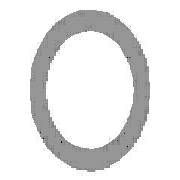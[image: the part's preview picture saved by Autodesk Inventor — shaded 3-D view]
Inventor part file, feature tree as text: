
AUTODESK INVENTOR PART (.ipt)
format: ipt  version: 2024.3 (Build 283343000, 343)  size: 162,304 bytes
history: native  units: mm (DEFAULTED — no unit token found)
features: other x5, sweep x1, sketch x1, plane x1
ambient origin geometry x8: Origin, YZ Plane, XZ Plane, XY Plane, X Axis, Y Axis, Z Axis, Center Point
bodies: Solid1 (feature_tree), Body (feature_tree)
feature tree (8):
  parser-record x1  (decoder bookkeeping rows leaked as tree rows — omitted from the tree; the rows remain in map.json)
  other  "Driven Length"
  other  "Start Plane"
  other  "End Plane"
  sweep  "Sweep Path"
  other  "Orientation Work Plane"
  sketch  "Sketch3"  dims[d0=42.4mm d1=2.0mm d4=-0.0mm d5=157.079633mm d6=90.0deg d7=157.079633mm d8=0.0mm d9=0.0mm]
  plane  "Work Plane3"
